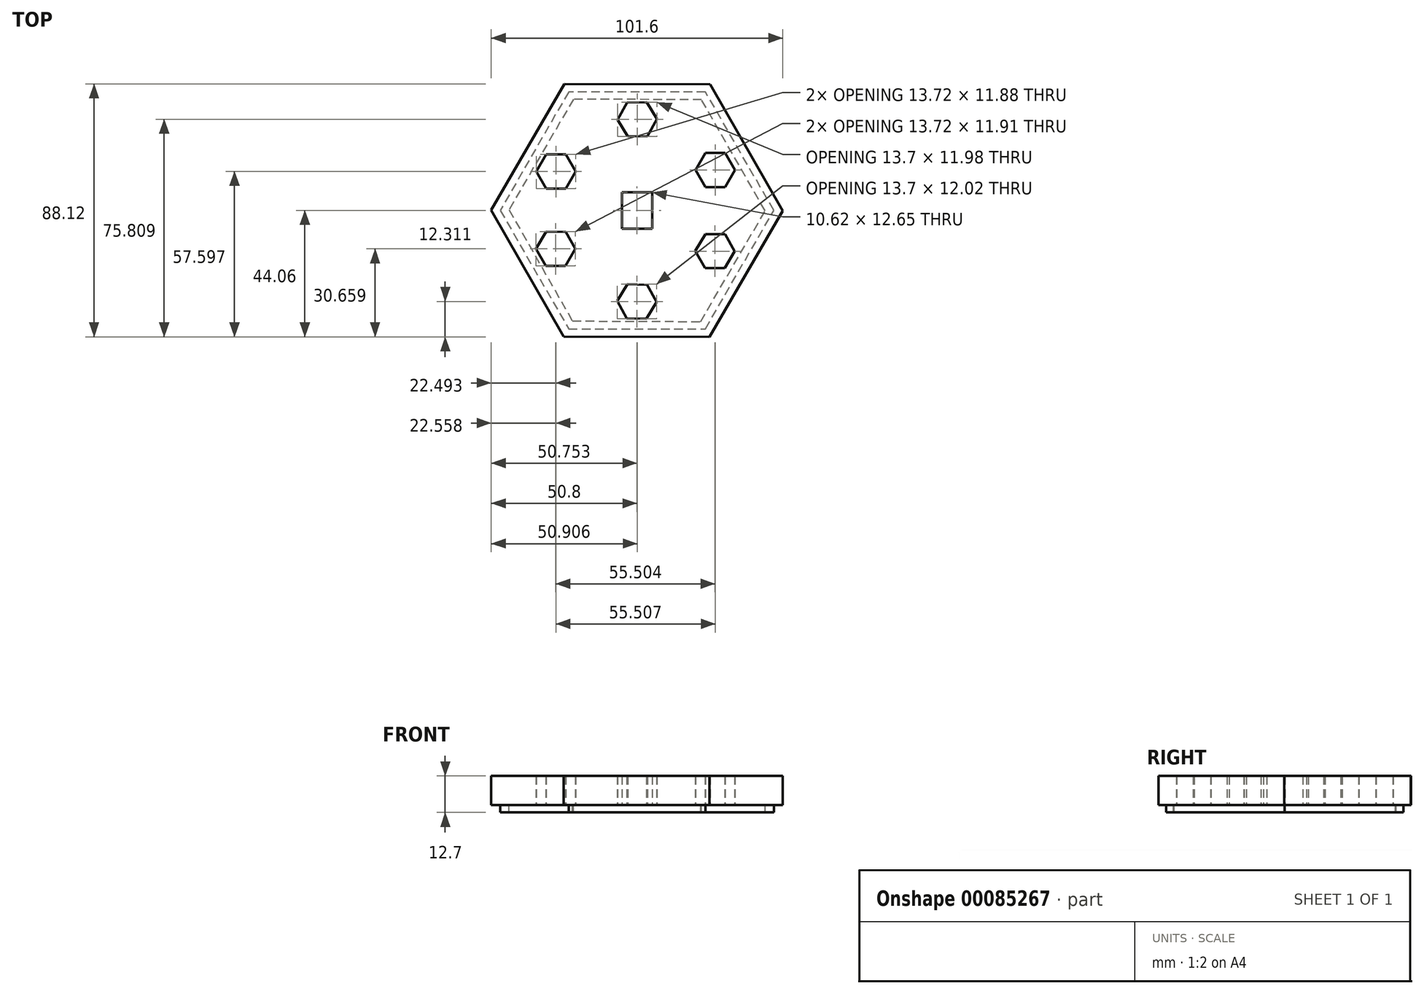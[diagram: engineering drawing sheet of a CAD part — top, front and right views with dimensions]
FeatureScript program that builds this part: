
annotation { "Feature Type Name" : "Feature", "Feature Type Description" : "" }
export const myFeature = defineFeature(function(context is Context, id is Id, definition is map)
    precondition{}
    {
        {
            var Q0;
            Q0=qCreatedBy(makeId("Top.planeOp"),FACE);
            var sketch = newSketch(context, id + "F0", { "sketchPlane" : qUnion([Q0])});
            skPoint(sketch, "E0.0.midPoint", {"position": v(50.43, -27.01) * mm});
            skLineSegment(sketch, "E1.bottom", {"start": v(5.31, -6.33) * mm, "end": v(-5.3, -6.33) * mm});
            skLineSegment(sketch, "E1.top", {"start": v(5.31, 6.33) * mm, "end": v(-5.3, 6.33) * mm});
            skLineSegment(sketch, "E1.left", {"start": v(5.31, -6.33) * mm, "end": v(5.31, 6.32) * mm});
            skLineSegment(sketch, "E1.right", {"start": v(-5.3, -6.33) * mm, "end": v(-5.3, 6.32) * mm});
            skPoint(sketch, "E1.middle", {"position": v(0, 0) * mm});
            skPoint(sketch, "E2.orphan", {"position": v(47.9, 39.24) * mm});
            skPoint(sketch, "E3.orphan", {"position": v(61.62, -6.13) * mm});
            skPoint(sketch, "E4.orphan", {"position": v(39.24, -47.9) * mm});
            skPoint(sketch, "E5.orphan", {"position": v(6.13, 61.62) * mm});
            skCircle(sketch, "E6.cCircle", {"center": v(0, 0) * mm, "radius": 44 * mm, "construction": true});
            skLineSegment(sketch, "E6.0", {"start": v(25.5, 43.93) * mm, "end": v(50.8, -0.12) * mm});
            skLineSegment(sketch, "E6.1", {"start": v(50.8, -0.12) * mm, "end": v(25.3, -44.06) * mm});
            skLineSegment(sketch, "E6.2", {"start": v(25.3, -44.06) * mm, "end": v(-25.5, -43.93) * mm});
            skLineSegment(sketch, "E6.3", {"start": v(-25.5, -43.93) * mm, "end": v(-50.8, 0.12) * mm});
            skLineSegment(sketch, "E6.4", {"start": v(-50.8, 0.12) * mm, "end": v(-25.3, 44.06) * mm});
            skLineSegment(sketch, "E6.5", {"start": v(-25.3, 44.06) * mm, "end": v(25.5, 43.93) * mm});
            skPoint(sketch, "E6.0.midPoint", {"position": v(38.15, 21.9) * mm});
            skCircle(sketch, "E7.cCircle", {"center": v(0.1, 31.75) * mm, "radius": 5.93 * mm, "construction": true});
            skPoint(sketch, "E7.cCircle.centerSnap0", {"position": v(0.1, 44) * mm});
            skLineSegment(sketch, "E7.0", {"start": v(-3.42, 37.62) * mm, "end": v(3.42, 37.74) * mm});
            skLineSegment(sketch, "E7.1", {"start": v(3.42, 37.74) * mm, "end": v(6.95, 31.87) * mm});
            skLineSegment(sketch, "E7.2", {"start": v(6.95, 31.87) * mm, "end": v(3.64, 25.88) * mm});
            skLineSegment(sketch, "E7.3", {"start": v(3.64, 25.88) * mm, "end": v(-3.21, 25.76) * mm});
            skLineSegment(sketch, "E7.4", {"start": v(-3.21, 25.76) * mm, "end": v(-6.74, 31.63) * mm});
            skLineSegment(sketch, "E7.5", {"start": v(-6.74, 31.63) * mm, "end": v(-3.42, 37.62) * mm});
            skPoint(sketch, "E7.0.midPoint", {"position": v(0, 37.68) * mm});
            skCircle(sketch, "E8.cCircle", {"center": v(27.27, 14.07) * mm, "radius": 5.94 * mm, "construction": true});
            skLineSegment(sketch, "E8.0", {"start": v(30.7, 8.13) * mm, "end": v(23.84, 8.13) * mm});
            skLineSegment(sketch, "E8.1", {"start": v(23.84, 8.13) * mm, "end": v(20.4, 14.07) * mm});
            skLineSegment(sketch, "E8.2", {"start": v(20.4, 14.07) * mm, "end": v(23.84, 20.01) * mm});
            skLineSegment(sketch, "E8.3", {"start": v(23.84, 20.01) * mm, "end": v(30.7, 20.01) * mm});
            skLineSegment(sketch, "E8.4", {"start": v(30.7, 20.01) * mm, "end": v(34.12, 14.07) * mm});
            skLineSegment(sketch, "E8.5", {"start": v(34.12, 14.07) * mm, "end": v(30.7, 8.13) * mm});
            skPoint(sketch, "E8.0.midPoint", {"position": v(27.27, 8.13) * mm});
            skCircle(sketch, "E9.cCircle", {"center": v(-28.24, 13.54) * mm, "radius": 5.94 * mm, "construction": true});
            skLineSegment(sketch, "E9.0", {"start": v(-24.81, 7.6) * mm, "end": v(-31.67, 7.6) * mm});
            skLineSegment(sketch, "E9.1", {"start": v(-31.67, 7.6) * mm, "end": v(-35.1, 13.54) * mm});
            skLineSegment(sketch, "E9.2", {"start": v(-35.1, 13.54) * mm, "end": v(-31.67, 19.48) * mm});
            skLineSegment(sketch, "E9.3", {"start": v(-31.67, 19.48) * mm, "end": v(-24.81, 19.48) * mm});
            skLineSegment(sketch, "E9.4", {"start": v(-24.81, 19.48) * mm, "end": v(-21.38, 13.54) * mm});
            skLineSegment(sketch, "E9.5", {"start": v(-21.38, 13.54) * mm, "end": v(-24.81, 7.6) * mm});
            skPoint(sketch, "E9.0.midPoint", {"position": v(-28.24, 7.6) * mm});
            skLineSegment(sketch, "E10.MirrorCS", {"start": v(20.34, -14.17) * mm, "end": v(23.74, -20.13) * mm});
            skLineSegment(sketch, "E11.MirrorCS", {"start": v(23.74, -20.13) * mm, "end": v(30.6, -20.16) * mm});
            skLineSegment(sketch, "E12.MirrorCS", {"start": v(30.6, -20.16) * mm, "end": v(34.06, -14.24) * mm});
            skLineSegment(sketch, "E13.MirrorCS", {"start": v(34.06, -14.24) * mm, "end": v(30.65, -8.28) * mm});
            skPoint(sketch, "E14.MirrorP", {"position": v(27.23, -8.27) * mm});
            skLineSegment(sketch, "E15.MirrorCS", {"start": v(23.8, -8.25) * mm, "end": v(20.34, -14.17) * mm});
            skLineSegment(sketch, "E16.MirrorCS", {"start": v(30.65, -8.28) * mm, "end": v(23.8, -8.25) * mm});
            skCircle(sketch, "E17.MirrorC", {"center": v(27.2, -14.2) * mm, "radius": 5.94 * mm, "construction": true});
            skLineSegment(sketch, "E18.MirrorCS", {"start": v(3.51, -25.9) * mm, "end": v(-3.34, -25.74) * mm});
            skLineSegment(sketch, "E19.MirrorCS", {"start": v(6.8, -31.9) * mm, "end": v(3.51, -25.9) * mm});
            skLineSegment(sketch, "E20.MirrorCS", {"start": v(3.24, -37.76) * mm, "end": v(6.8, -31.9) * mm});
            skCircle(sketch, "E21.MirrorC", {"center": v(-0.05, -31.75) * mm, "radius": 5.93 * mm, "construction": true});
            skPoint(sketch, "E22.MirrorP", {"position": v(-0.18, -37.68) * mm});
            skLineSegment(sketch, "E23.MirrorCS", {"start": v(-3.6, -37.6) * mm, "end": v(3.24, -37.76) * mm});
            skLineSegment(sketch, "E24.MirrorCS", {"start": v(-3.34, -25.74) * mm, "end": v(-6.9, -31.6) * mm});
            skLineSegment(sketch, "E25.MirrorCS", {"start": v(-6.9, -31.6) * mm, "end": v(-3.6, -37.6) * mm});
            skLineSegment(sketch, "E26.MirrorCS", {"start": v(-21.45, -13.43) * mm, "end": v(-24.85, -7.48) * mm});
            skCircle(sketch, "E27.MirrorC", {"center": v(-28.3, -13.4) * mm, "radius": 5.94 * mm, "construction": true});
            skLineSegment(sketch, "E28.MirrorCS", {"start": v(-31.7, -7.45) * mm, "end": v(-35.16, -13.37) * mm});
            skPoint(sketch, "E29.MirrorP", {"position": v(-28.28, -7.46) * mm});
            skLineSegment(sketch, "E30.MirrorCS", {"start": v(-24.85, -7.48) * mm, "end": v(-31.7, -7.45) * mm});
            skLineSegment(sketch, "E31.MirrorCS", {"start": v(-24.9, -19.36) * mm, "end": v(-21.45, -13.43) * mm});
            skLineSegment(sketch, "E32.MirrorCS", {"start": v(-31.76, -19.32) * mm, "end": v(-24.9, -19.36) * mm});
            skLineSegment(sketch, "E33.MirrorCS", {"start": v(-35.16, -13.37) * mm, "end": v(-31.76, -19.32) * mm});
            skSolve(sketch);
        }
        {
            var Q0;
            Q0=makeQuery(id+"F0.imprint","IMPRINT",FACE,{"disambiguationData":[TD([[makeQuery(id+"F0.imprint","IMPRINT",EDGE,{"derivedFrom":sQuery(id+"F0.wireOp",EDGE,"E1.bottom")}),1.0]])]});
            extrude(context, id + "F1", {"entities" : qUnion([Q0]), "depth" : 10.16 * mm});
        }
        {
            var Q0;
            Q0=makeQuery(id+"F1.opExtrude","CAP_FACE",FACE,{"disambiguationData":[OSD([sQuery(id+"F0.wireOp",EDGE,"E1.bottom"),sQuery(id+"F0.wireOp",EDGE,"E1.top"),sQuery(id+"F0.wireOp",EDGE,"E1.left"),sQuery(id+"F0.wireOp",EDGE,"E1.right"),sQuery(id+"F0.wireOp",EDGE,"E6.0"),sQuery(id+"F0.wireOp",EDGE,"E6.1"),sQuery(id+"F0.wireOp",EDGE,"E6.2"),sQuery(id+"F0.wireOp",EDGE,"E6.3"),sQuery(id+"F0.wireOp",EDGE,"E6.4"),sQuery(id+"F0.wireOp",EDGE,"E6.5"),sQuery(id+"F0.wireOp",EDGE,"E7.0"),sQuery(id+"F0.wireOp",EDGE,"E7.1"),sQuery(id+"F0.wireOp",EDGE,"E7.2"),sQuery(id+"F0.wireOp",EDGE,"E7.3"),sQuery(id+"F0.wireOp",EDGE,"E7.4"),sQuery(id+"F0.wireOp",EDGE,"E7.5"),sQuery(id+"F0.wireOp",EDGE,"E8.0"),sQuery(id+"F0.wireOp",EDGE,"E8.1"),sQuery(id+"F0.wireOp",EDGE,"E8.2"),sQuery(id+"F0.wireOp",EDGE,"E8.3"),sQuery(id+"F0.wireOp",EDGE,"E8.4"),sQuery(id+"F0.wireOp",EDGE,"E8.5"),sQuery(id+"F0.wireOp",EDGE,"E9.0"),sQuery(id+"F0.wireOp",EDGE,"E9.1"),sQuery(id+"F0.wireOp",EDGE,"E9.2"),sQuery(id+"F0.wireOp",EDGE,"E9.3"),sQuery(id+"F0.wireOp",EDGE,"E9.4"),sQuery(id+"F0.wireOp",EDGE,"E9.5"),sQuery(id+"F0.wireOp",EDGE,"E10.MirrorCS"),sQuery(id+"F0.wireOp",EDGE,"E11.MirrorCS"),sQuery(id+"F0.wireOp",EDGE,"E12.MirrorCS"),sQuery(id+"F0.wireOp",EDGE,"E13.MirrorCS"),sQuery(id+"F0.wireOp",EDGE,"E15.MirrorCS"),sQuery(id+"F0.wireOp",EDGE,"E16.MirrorCS"),sQuery(id+"F0.wireOp",EDGE,"E18.MirrorCS"),sQuery(id+"F0.wireOp",EDGE,"E19.MirrorCS"),sQuery(id+"F0.wireOp",EDGE,"E23.MirrorCS"),sQuery(id+"F0.wireOp",EDGE,"E20.MirrorCS"),sQuery(id+"F0.wireOp",EDGE,"E24.MirrorCS"),sQuery(id+"F0.wireOp",EDGE,"E25.MirrorCS"),sQuery(id+"F0.wireOp",EDGE,"E30.MirrorCS"),sQuery(id+"F0.wireOp",EDGE,"E26.MirrorCS"),sQuery(id+"F0.wireOp",EDGE,"E28.MirrorCS"),sQuery(id+"F0.wireOp",EDGE,"E31.MirrorCS"),sQuery(id+"F0.wireOp",EDGE,"E32.MirrorCS"),sQuery(id+"F0.wireOp",EDGE,"E33.MirrorCS")])],"isStart":true});
            var sketch = newSketch(context, id + "F2", { "sketchPlane" : qUnion([Q0])});
            skPoint(sketch, "E34.cCircle.perimeterSnap0", {"position": v(-33.39, -16.5) * mm});
            skLineSegment(sketch, "E34.0", {"start": v(-22.14, -38.75) * mm, "end": v(-44.63, -0.2) * mm});
            skLineSegment(sketch, "E34.1", {"start": v(-44.63, -0.2) * mm, "end": v(-22.49, 38.55) * mm});
            skLineSegment(sketch, "E34.2", {"start": v(-22.49, 38.55) * mm, "end": v(22.14, 38.75) * mm});
            skLineSegment(sketch, "E34.3", {"start": v(22.14, 38.75) * mm, "end": v(44.63, 0.2) * mm});
            skLineSegment(sketch, "E34.4", {"start": v(44.63, 0.2) * mm, "end": v(22.49, -38.55) * mm});
            skLineSegment(sketch, "E34.5", {"start": v(22.49, -38.55) * mm, "end": v(-22.14, -38.75) * mm});
            skPoint(sketch, "E34.0.midPoint", {"position": v(-33.39, -19.48) * mm});
            skPoint(sketch, "E34.0.midPoint.positionSnap0", {"position": v(-33.39, -16.5) * mm});
            skLineSegment(sketch, "E35.0", {"start": v(23.83, -41.28) * mm, "end": v(-23.83, -41.28) * mm});
            skLineSegment(sketch, "E35.1", {"start": v(-23.83, -41.28) * mm, "end": v(-47.66, 0) * mm});
            skLineSegment(sketch, "E35.2", {"start": v(-47.66, 0) * mm, "end": v(-23.83, 41.28) * mm});
            skLineSegment(sketch, "E35.3", {"start": v(-23.83, 41.28) * mm, "end": v(23.83, 41.28) * mm});
            skLineSegment(sketch, "E35.4", {"start": v(23.83, 41.28) * mm, "end": v(47.66, 0) * mm});
            skLineSegment(sketch, "E35.5", {"start": v(47.66, 0) * mm, "end": v(23.83, -41.28) * mm});
            skPoint(sketch, "E35.0.midPoint", {"position": v(0, -41.28) * mm});
            skPoint(sketch, "E34.cCircle.center.orphan", {"position": v(0, 0) * mm});
            skLineSegment(sketch, "E36", {"start": v(47.66, 0) * mm, "end": v(44.63, 0.2) * mm});
            skLineSegment(sketch, "E37", {"start": v(23.83, 41.28) * mm, "end": v(22.14, 38.75) * mm});
            skLineSegment(sketch, "E38", {"start": v(-22.49, 38.55) * mm, "end": v(-23.83, 41.28) * mm});
            skLineSegment(sketch, "E39", {"start": v(-44.63, -0.2) * mm, "end": v(-47.66, 0) * mm});
            skLineSegment(sketch, "E40", {"start": v(-22.14, -38.75) * mm, "end": v(-23.83, -41.28) * mm});
            skLineSegment(sketch, "E41", {"start": v(23.83, -41.28) * mm, "end": v(22.49, -38.55) * mm});
            skLineSegment(sketch, "E42", {"start": v(-23.83, 41.28) * mm, "end": v(-25.5, 43.93) * mm});
            skSolve(sketch);
        }
        {
            var Q0;
            Q0=makeQuery(id+"F2.imprint","IMPRINT",FACE,{"disambiguationData":[TD([[makeQuery(id+"F2.imprint","IMPRINT",EDGE,{"derivedFrom":sQuery(id+"F2.wireOp",EDGE,"E34.4")}),1.0]])]});
            extrude(context, id + "F3", {"entities" : qUnion([Q0]), "operationType" : NewBodyOperationType.ADD, "depth" : 2.54 * mm});
        }
        {
            var Q0;
            Q0=makeQuery(id+"F2.imprint","IMPRINT",FACE,{"disambiguationData":[TD([[makeQuery(id+"F2.imprint","IMPRINT",EDGE,{"derivedFrom":sQuery(id+"F2.wireOp",EDGE,"E34.3")}),1.0]])]});
            extrude(context, id + "F4", {"entities" : qUnion([Q0]), "operationType" : NewBodyOperationType.ADD, "depth" : 2.54 * mm});
        }
        {
            var Q0;
            Q0=makeQuery(id+"F2.imprint","IMPRINT",FACE,{"disambiguationData":[TD([[makeQuery(id+"F2.imprint","IMPRINT",EDGE,{"derivedFrom":sQuery(id+"F2.wireOp",EDGE,"E34.2")}),1.0]])]});
            extrude(context, id + "F5", {"entities" : qUnion([Q0]), "operationType" : NewBodyOperationType.ADD, "depth" : 2.54 * mm});
        }
        {
            var Q0;
            Q0=makeQuery(id+"F2.imprint","IMPRINT",FACE,{"disambiguationData":[TD([[makeQuery(id+"F2.imprint","IMPRINT",EDGE,{"derivedFrom":sQuery(id+"F2.wireOp",EDGE,"E34.1")}),1.0]])]});
            extrude(context, id + "F6", {"entities" : qUnion([Q0]), "operationType" : NewBodyOperationType.ADD, "depth" : 2.54 * mm});
        }
        {
            var Q0;
            Q0=makeQuery(id+"F2.imprint","IMPRINT",FACE,{"disambiguationData":[TD([[makeQuery(id+"F2.imprint","IMPRINT",EDGE,{"derivedFrom":sQuery(id+"F2.wireOp",EDGE,"E34.0")}),1.0]])]});
            extrude(context, id + "F7", {"entities" : qUnion([Q0]), "operationType" : NewBodyOperationType.ADD, "depth" : 2.54 * mm});
        }
        {
            var Q0;
            Q0=makeQuery(id+"F2.imprint","IMPRINT",FACE,{"disambiguationData":[TD([[makeQuery(id+"F2.imprint","IMPRINT",EDGE,{"derivedFrom":sQuery(id+"F2.wireOp",EDGE,"E34.5")}),1.0]])]});
            extrude(context, id + "F8", {"entities" : qUnion([Q0]), "operationType" : NewBodyOperationType.ADD, "depth" : 2.54 * mm});
        }
    });
